# Revit family: Legrand_GTL_bac_métal_Drivia_18_modules_1_travée
name_source: partatom
category: Equipement électrique
revit_build: Autodesk Revit 2018 (Build: 20170223_1515(x64)
units: mm (PartAtom-declared; Revit-internal decimal feet)

## family parameters
Basée sur le plan de construction = Non
Configuration du panneau = Deux colonnes, circuits au sein
Cote de connecteur circulaire = Utiliser le diamètre
Couper avec des vides une fois chargée = Non
Numéro OmniClass = 23.80.30.11.17
Partagée = Non
Point de calcul de pièce = Non
Titre OmniClass = Distribution Boards and Control Panels
Toujours verticalement = Oui
Type d'élément = Tableau de raccordement

## types (3) — shared parameters
Conditions Générale d'Utilisation = https://export.legrand.com
ETIM Class 6.0 = EC000214
Fabricant = Legrand
Image du type = bac_encastr_drivia_401443_pw_231681_pz_1.jpg
Matière = acier électro zingué
RAL = 9003
porte = Oui
trappe d'accés = Oui

## per-type parameters (varying)
| type | Description | bac 401444 | bac 401445 | bac 401446 | porte 401454 | porte 401455 | porte 401456 |
| Legrand Bac GTL encastrée Drivia 18 modules 1 travées H=1100 | 401446 + 401456  Legrand Bac GTL encastrée Drivia 18 modules 1 travées H=1100 | Non | Non | Oui | Non | Non | Oui |
| Legrand Bac GTL encastrée Drivia 18 modules 1 travées H=975 | 401445 + 401455  Legrand Bac GTL encastrée Drivia 18 modules 1 travées H=975 | Non | Oui | Non | Non | Oui | Non |
| Legrand Bac GTL encastrée Drivia 18 modules 1 travées H=850 | 401444 + 401454  Legrand Bac GTL encastrée Drivia 18 modules 1 travées H=850 | Oui | Non | Non | Oui | Non | Non |
